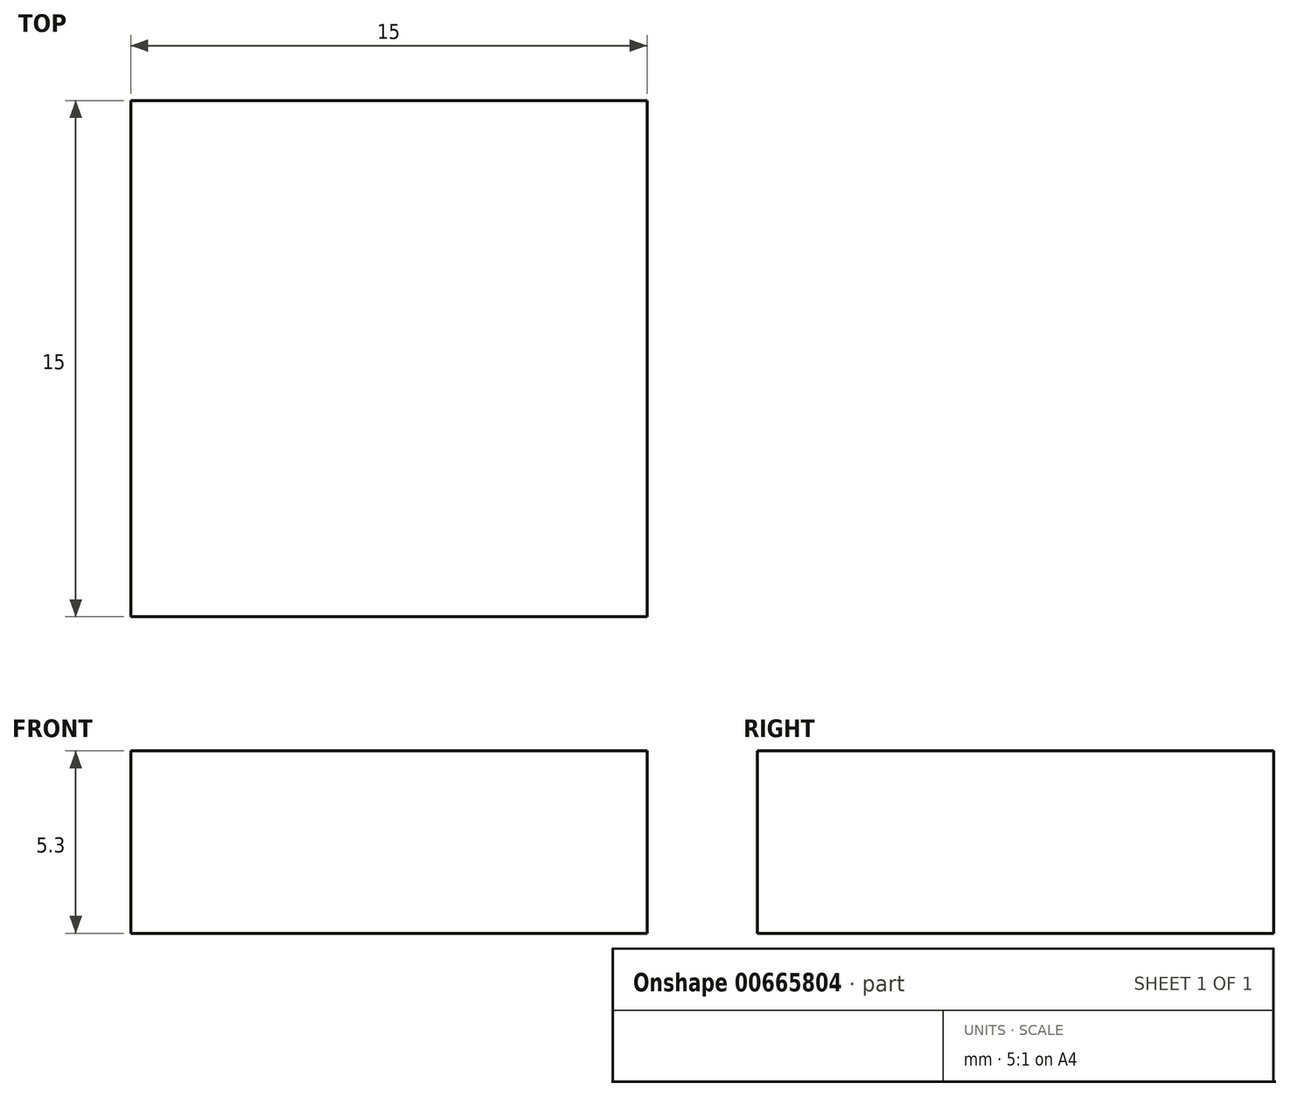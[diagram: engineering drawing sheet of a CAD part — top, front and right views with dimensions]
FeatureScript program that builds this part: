
annotation { "Feature Type Name" : "Feature", "Feature Type Description" : "" }
export const myFeature = defineFeature(function(context is Context, id is Id, definition is map)
    precondition{}
    {
        {
            var Q0;
            Q0=qCreatedBy(makeId("Top.planeOp"),FACE);
            var sketch = newSketch(context, id + "F0", { "sketchPlane" : qUnion([Q0])});
            skLineSegment(sketch, "E0.bottom", {"start": v(7.5, -7.5) * mm, "end": v(-7.5, -7.5) * mm});
            skLineSegment(sketch, "E0.top", {"start": v(7.5, 7.5) * mm, "end": v(-7.5, 7.5) * mm});
            skLineSegment(sketch, "E0.left", {"start": v(7.5, -7.5) * mm, "end": v(7.5, 7.5) * mm});
            skLineSegment(sketch, "E0.right", {"start": v(-7.5, -7.5) * mm, "end": v(-7.5, 7.5) * mm});
            skPoint(sketch, "E0.middle", {"position": v(0, 0) * mm});
            skSolve(sketch);
        }
        {
            var Q0;
            Q0=makeQuery(id+"F0.imprint","IMPRINT",FACE,{"disambiguationData":[TD([[makeQuery(id+"F0.imprint","IMPRINT",EDGE,{"derivedFrom":sQuery(id+"F0.wireOp",EDGE,"E0.bottom")}),-1.0]])]});
            extrude(context, id + "F1", {"entities" : qUnion([Q0]), "depth" : 5.3 * mm, "offsetDistance" : 25 * mm});
        }
    });
